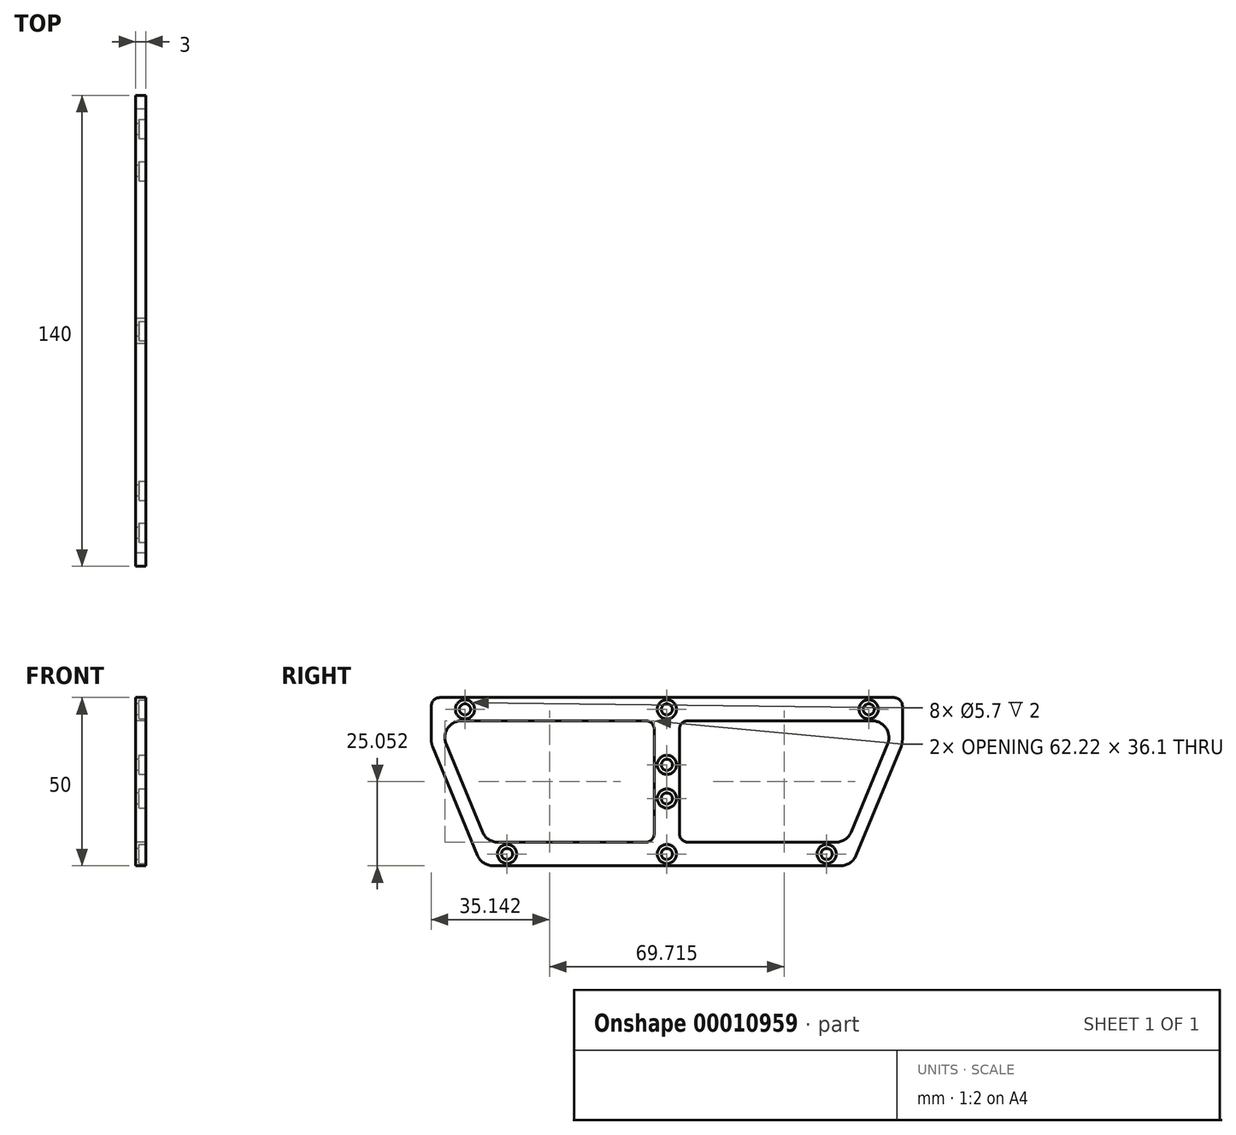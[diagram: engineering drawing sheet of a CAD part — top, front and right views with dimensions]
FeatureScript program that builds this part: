
annotation { "Feature Type Name" : "Feature", "Feature Type Description" : "" }
export const myFeature = defineFeature(function(context is Context, id is Id, definition is map)
    precondition{}
    {
        {
            var Q0;
            Q0=qCreatedBy(makeId("Right.planeOp"),FACE);
            var sketch = newSketch(context, id + "F0", { "sketchPlane" : qUnion([Q0])});
            skLineSegment(sketch, "E0.bottom", {"start": v(-70, 0) * mm, "end": v(70, 0) * mm, "construction": true});
            skLineSegment(sketch, "E0.top", {"start": v(-70, 60) * mm, "end": v(70, 60) * mm, "construction": true});
            skLineSegment(sketch, "E0.left", {"start": v(-70, 0) * mm, "end": v(-70, 60) * mm, "construction": true});
            skLineSegment(sketch, "E0.right", {"start": v(70, 0) * mm, "end": v(70, 60) * mm, "construction": true});
            skLineSegment(sketch, "E1.bottom", {"start": v(-67.5, 0) * mm, "end": v(0, 0) * mm});
            skLineSegment(sketch, "E2", {"start": v(0, 0) * mm, "end": v(0, -1.85) * mm});
            skLineSegment(sketch, "E3", {"start": v(-6.25, -6.9) * mm, "end": v(-60.99, -6.9) * mm});
            skLineSegment(sketch, "E4", {"start": v(-65.61, -13.8) * mm, "end": v(-54.84, -39.9) * mm});
            skLineSegment(sketch, "E5", {"start": v(-50.22, -43) * mm, "end": v(-6.25, -43) * mm});
            skLineSegment(sketch, "E6", {"start": v(0, -43) * mm, "end": v(0, -44.85) * mm});
            skLineSegment(sketch, "E7", {"start": v(0, -50) * mm, "end": v(-51.65, -50) * mm});
            skLineSegment(sketch, "E8", {"start": v(-56.28, -46.9) * mm, "end": v(-69.62, -14.57) * mm});
            skLineSegment(sketch, "E9", {"start": v(-70, -12.66) * mm, "end": v(-70, -2.5) * mm});
            skPoint(sketch, "E10.visualSharp", {"position": v(-68.46, -6.9) * mm});
            skArc(sketch, "E10.filletArc", {"start": v(-60.99, -6.9) * mm, "mid": v(-65.15, -9.12) * mm, "end": v(-65.61, -13.8) * mm});
            skPoint(sketch, "E11.visualSharp", {"position": v(-70, -13.66) * mm});
            skArc(sketch, "E11.filletArc", {"start": v(-70, -12.66) * mm, "mid": v(-69.9, -13.64) * mm, "end": v(-69.62, -14.57) * mm});
            skPoint(sketch, "E12.visualSharp", {"position": v(-55, -50) * mm});
            skArc(sketch, "E12.filletArc", {"start": v(-56.28, -46.9) * mm, "mid": v(-54.43, -49.16) * mm, "end": v(-51.65, -50) * mm});
            skPoint(sketch, "E13.visualSharp", {"position": v(-53.56, -43) * mm});
            skArc(sketch, "E13.filletArc", {"start": v(-54.84, -39.9) * mm, "mid": v(-53, -42.16) * mm, "end": v(-50.22, -43) * mm});
            skLineSegment(sketch, "E14", {"start": v(-60.22, -26.86) * mm, "end": v(-63.92, -28.38) * mm, "construction": true});
            skLineSegment(sketch, "E15.left", {"start": v(0, -6.9) * mm, "end": v(0, -18.35) * mm});
            skLineSegment(sketch, "E15.right", {"start": v(-3.75, -9.4) * mm, "end": v(-3.75, -40.5) * mm});
            skPoint(sketch, "E16.visualSharp", {"position": v(-3.75, -6.9) * mm});
            skArc(sketch, "E16.filletArc", {"start": v(-3.75, -9.4) * mm, "mid": v(-4.48, -7.63) * mm, "end": v(-6.25, -6.9) * mm});
            skPoint(sketch, "E17.visualSharp", {"position": v(-3.75, -43) * mm});
            skArc(sketch, "E17.filletArc", {"start": v(-6.25, -43) * mm, "mid": v(-4.48, -42.27) * mm, "end": v(-3.75, -40.5) * mm});
            skCircle(sketch, "E18", {"center": v(-60, -3.5) * mm, "radius": 1.65 * mm});
            skLineSegment(sketch, "E19", {"start": v(-60, -3.5) * mm, "end": v(0, -3.5) * mm, "construction": true});
            skArc(sketch, "E20", {"start": v(0, -1.85) * mm, "mid": v(-1.65, -3.5) * mm, "end": v(0, -5.15) * mm});
            skCircle(sketch, "E21", {"center": v(-47.5, -46.5) * mm, "radius": 1.65 * mm});
            skLineSegment(sketch, "E22", {"start": v(-47.5, -46.5) * mm, "end": v(0, -46.5) * mm, "construction": true});
            skArc(sketch, "E23", {"start": v(0, -44.85) * mm, "mid": v(-1.65, -46.5) * mm, "end": v(0, -48.15) * mm});
            skPoint(sketch, "E24.visualSharp", {"position": v(-70, 0) * mm});
            skArc(sketch, "E24.filletArc", {"start": v(-67.5, 0) * mm, "mid": v(-69.27, -0.73) * mm, "end": v(-70, -2.5) * mm});
            skLineSegment(sketch, "E25", {"start": v(0, -46.5) * mm, "end": v(0, -46.5) * mm});
            skLineSegment(sketch, "E26.trimOffspring", {"start": v(0, -5.15) * mm, "end": v(0, -6.9) * mm});
            skLineSegment(sketch, "E27.trimOffspring", {"start": v(0, -48.15) * mm, "end": v(0, -50) * mm});
            skArc(sketch, "E28", {"start": v(0, -28.35) * mm, "mid": v(-1.65, -30) * mm, "end": v(0, -31.65) * mm});
            skLineSegment(sketch, "E29.trimOffspring", {"start": v(0, -21.65) * mm, "end": v(0, -28.35) * mm});
            skLineSegment(sketch, "E30.trimOffspring", {"start": v(0, -31.65) * mm, "end": v(0, -44.85) * mm});
            skArc(sketch, "E31", {"start": v(0, -18.35) * mm, "mid": v(-1.65, -20) * mm, "end": v(0, -21.65) * mm});
            skPoint(sketch, "E32", {"position": v(0, -25) * mm});
            skSolve(sketch);
        }
        {
            var Q0;
            Q0 = qSketchRegion(id + "F0", true);
            extrude(context, id + "F1", {"entities" : qUnion([Q0]), "depth" : 3 * mm});
        }
        {
            var Q0;
            Q0=makeQuery(id+"F1.opExtrude","CAP_FACE",FACE,{"disambiguationData":[OSD([sQuery(id+"F0.wireOp",EDGE,"E1.bottom"),sQuery(id+"F0.wireOp",EDGE,"E2"),sQuery(id+"F0.wireOp",EDGE,"E3"),sQuery(id+"F0.wireOp",EDGE,"E4"),sQuery(id+"F0.wireOp",EDGE,"E5"),sQuery(id+"F0.wireOp",EDGE,"E6"),sQuery(id+"F0.wireOp",EDGE,"E7"),sQuery(id+"F0.wireOp",EDGE,"E8"),sQuery(id+"F0.wireOp",EDGE,"E9"),sQuery(id+"F0.wireOp",EDGE,"E10.filletArc"),sQuery(id+"F0.wireOp",EDGE,"E11.filletArc"),sQuery(id+"F0.wireOp",EDGE,"E12.filletArc"),sQuery(id+"F0.wireOp",EDGE,"E13.filletArc"),sQuery(id+"F0.wireOp",EDGE,"E15.left"),sQuery(id+"F0.wireOp",EDGE,"E15.right"),sQuery(id+"F0.wireOp",EDGE,"E16.filletArc"),sQuery(id+"F0.wireOp",EDGE,"E17.filletArc"),sQuery(id+"F0.wireOp",EDGE,"E18"),sQuery(id+"F0.wireOp",EDGE,"E20"),sQuery(id+"F0.wireOp",EDGE,"E21"),sQuery(id+"F0.wireOp",EDGE,"E23"),sQuery(id+"F0.wireOp",EDGE,"E24.filletArc")])],"isStart":false});
            var sketch = newSketch(context, id + "F2", { "sketchPlane" : qUnion([Q0])});
            skCircle(sketch, "E33", {"center": v(-60, -3.5) * mm, "radius": 2.85 * mm});
            skCircle(sketch, "E34", {"center": v(0, -3.5) * mm, "radius": 2.85 * mm});
            skCircle(sketch, "E35", {"center": v(0, -46.5) * mm, "radius": 2.85 * mm});
            skCircle(sketch, "E36", {"center": v(-47.5, -46.5) * mm, "radius": 2.85 * mm});
            skCircle(sketch, "E37", {"center": v(0, -30) * mm, "radius": 2.85 * mm});
            skCircle(sketch, "E38", {"center": v(0, -20) * mm, "radius": 2.85 * mm});
            skSolve(sketch);
        }
        {
            var Q0;
            Q0 = qSketchRegion(id + "F2", true);
            extrude(context, id + "F3", {"entities" : qUnion([Q0]), "operationType" : NewBodyOperationType.REMOVE, "oppositeDirection" : true, "depth" : 2 * mm});
        }
        {
            var Q0;
            Q0=makeQuery(id+"F1.opExtrude","SWEPT_BODY",BODY,{"disambiguationData":[OSD([sQuery(id+"F0.wireOp",EDGE,"E1.bottom"),sQuery(id+"F0.wireOp",EDGE,"E2"),sQuery(id+"F0.wireOp",EDGE,"E3"),sQuery(id+"F0.wireOp",EDGE,"E4"),sQuery(id+"F0.wireOp",EDGE,"E5"),sQuery(id+"F0.wireOp",EDGE,"E6"),sQuery(id+"F0.wireOp",EDGE,"E7"),sQuery(id+"F0.wireOp",EDGE,"E8"),sQuery(id+"F0.wireOp",EDGE,"E9"),sQuery(id+"F0.wireOp",EDGE,"E10.filletArc"),sQuery(id+"F0.wireOp",EDGE,"E11.filletArc"),sQuery(id+"F0.wireOp",EDGE,"E12.filletArc"),sQuery(id+"F0.wireOp",EDGE,"E13.filletArc")])]});
            var Q1;
            Q1=qCreatedBy(makeId("Front.planeOp"),FACE);
            mirror(context, id + "F4", {"operationType" : NewBodyOperationType.ADD, "entities" : qUnion([Q0]), "mirrorPlane" : qUnion([Q1])});
        }
    });
